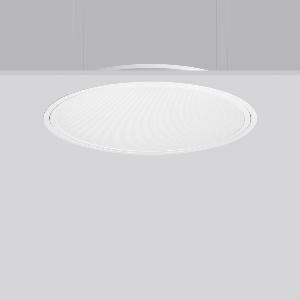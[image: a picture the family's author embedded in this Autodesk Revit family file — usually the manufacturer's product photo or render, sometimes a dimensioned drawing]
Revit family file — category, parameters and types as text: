
# Revit family: triona_round_e_312296_002_2_12_6a8b
name_source: partatom
category: Lighting Fixtures
units: mm (PartAtom-declared; Revit-internal decimal feet)

## family parameters
Cut with Voids When Loaded = No
Host = Face
Light Source = No
Part Type = Normal
Room Calculation Point = No
Round Connector Dimension = Use Diameter
Shared = No

## types (1)
- TuneableWhite 846 (1 x LED Modul 846, 3550 lm, 4600)
    Apparent Load = 40 VA
    CIE Flux Codes = 59 87 97 100 100
    Color Rendering = 80
    Color Temperature = 4600
    Default Elevation = 1800 mm
    Description = Series: TRIONA round
Decorative round LED recessed surface luminaire. Cover made of sheet steel, powder-coated. Frame made of aluminium, powder-coated. Recessed ring: aluminium extrusion profile, powder coated. Light emission through a diffuser in plastic, opal/prismatic. Lightguide and diffuser made of non-yellowing plastic (PMMA). Lateral light emission (RZB SIDELITE technology) for above-average homogeneous light distribution. Tunable white versions, dynamically adjustable from 2700 K to 6500 K. Suitable for installation in cavity ceilings. Tool-free mounting system thanks to the rocker arm mechanism (patent pending). Electronic ballast included. Very easy installation thanks to Plug+Play connection. Ideal for use as part of the Human Centric Lighting concept in connection with RZB light management systems. 
Colour: traffic white, matt (RAL 9016)
Diameter: 725 mm
Height: 2 mm
Cut-out diameter: 702 mm
Recess height: 100 mm
Luminaire: recess height: 89 mm
Lamp: LED
Socket: without socket
Colour temperature: 2700K - 6500K
Colour rendering index (CRI): 80
System power: 40 W
Rated luminous flux: 3550 lm
Luminous efficiency: 89 lm/W
System power 2: 42 W
Rated luminous flux 2: 3400 lm
Luminous efficiency 2: 81 lm/W
System power 3: 42 W
Rated luminous flux 3: 3400 lm
Luminous efficiency 3: 81 lm/W
Control gear: Converter, dimmable, DALI
Protection class: I
Type of protection: IP 40
    Height = 0 mm  [stored 0 ft]
    Lamp = 1 x LED Modul 846
    Lamp Light Flux = 3550 lm
    Lamp count = 1
    Length = 725 mm
    Lifetime = 50000 h
    Luminous efficacy = 89 lm/W
    Manufacturer = RZB
    ModVariant = No
    Model = 312296.002.2.12
    Mounting Place = Ceiling
    Mounting Type = Recessed
    Number of Poles = 1
    OnlyDefault = Yes
    Power Factor = 1
    Product Name = TRIONA round E
    Product group = Recessed modular luminaires
    ProductGroupID = 406
    Protection Class = Protection class I
    Protection Degree = IP 20
    RLX_Detail_Level = 1
    RLX_Emergency_Light_Flux = 0 lm
    RLX_Emergency_Type = 0
    RLX_Emergency_Type_DB = No
    RlxData = <blob elided: 36921 chars, md5=aed573a7>
    Socket = socket
    Standby Power = 0 W
    System Light Flux = 3550 lm
    System Power = 40 W
    Type Comments = TuneableWhite 846
    Type Image = 312296.002.12.jpg
    URL = http://relux.com
    VarID = tuneablewhite_846
    Voltage = 230 V
    Voltage Range = 220-240 V
    Weight = 0.00 kg
    Width = 0 mm  [stored 0 ft]

note: [stored X ft] marks values corroborated as IEEE doubles in the binary element streams (Revit-internal decimal feet)

## geometry (parser evidence)
native form markers: Blend x4, Sweep x11
no freeform markers — native parametric forms only
